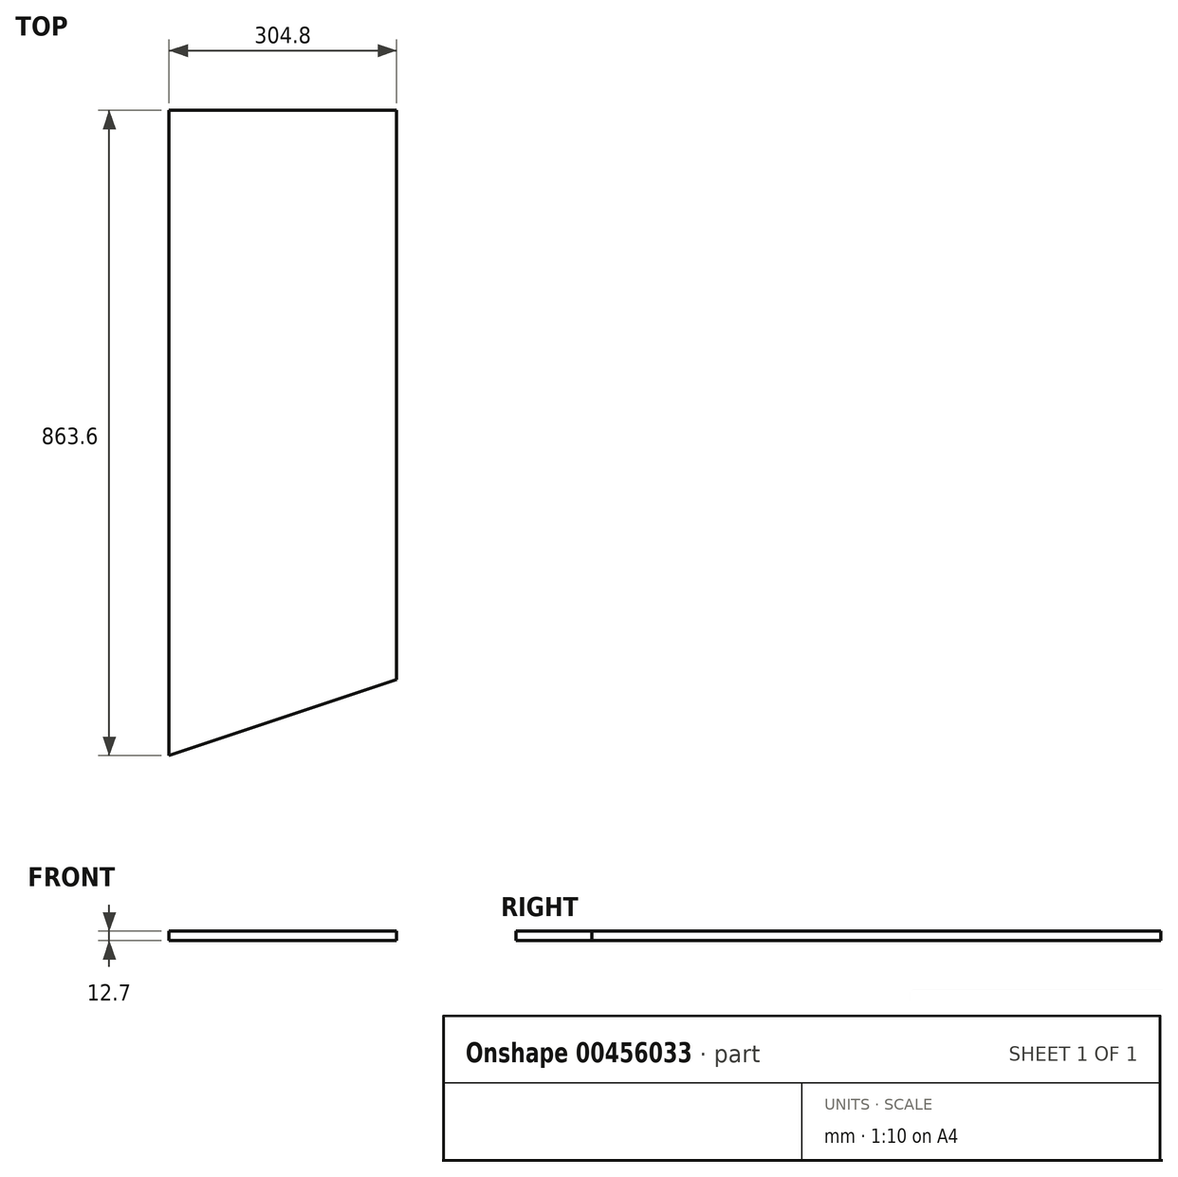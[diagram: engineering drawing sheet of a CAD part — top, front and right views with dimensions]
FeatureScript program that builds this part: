
annotation { "Feature Type Name" : "Feature", "Feature Type Description" : "" }
export const myFeature = defineFeature(function(context is Context, id is Id, definition is map)
    precondition{}
    {
        {
            var Q0;
            Q0=qCreatedBy(makeId("Top.planeOp"),FACE);
            var sketch = newSketch(context, id + "F0", { "sketchPlane" : qUnion([Q0])});
            skLineSegment(sketch, "E0.bottom", {"start": v(0, 0) * mm, "end": v(304.8, 0) * mm});
            skLineSegment(sketch, "E0.left", {"start": v(0, 0) * mm, "end": v(0, -863.6) * mm});
            skLineSegment(sketch, "E1", {"start": v(304.8, 0) * mm, "end": v(304.8, -762) * mm});
            skLineSegment(sketch, "E2", {"start": v(304.8, -762) * mm, "end": v(0, -863.6) * mm});
            skSolve(sketch);
        }
        {
            var Q0;
            Q0=makeQuery(id+"F0.imprint","IMPRINT",FACE,{"disambiguationData":[TD([[makeQuery(id+"F0.imprint","IMPRINT",EDGE,{"derivedFrom":sQuery(id+"F0.wireOp",EDGE,"E0.bottom")}),-1.0]])]});
            extrude(context, id + "F1", {"entities" : qUnion([Q0]), "depth" : 12.7 * mm});
        }
    });
